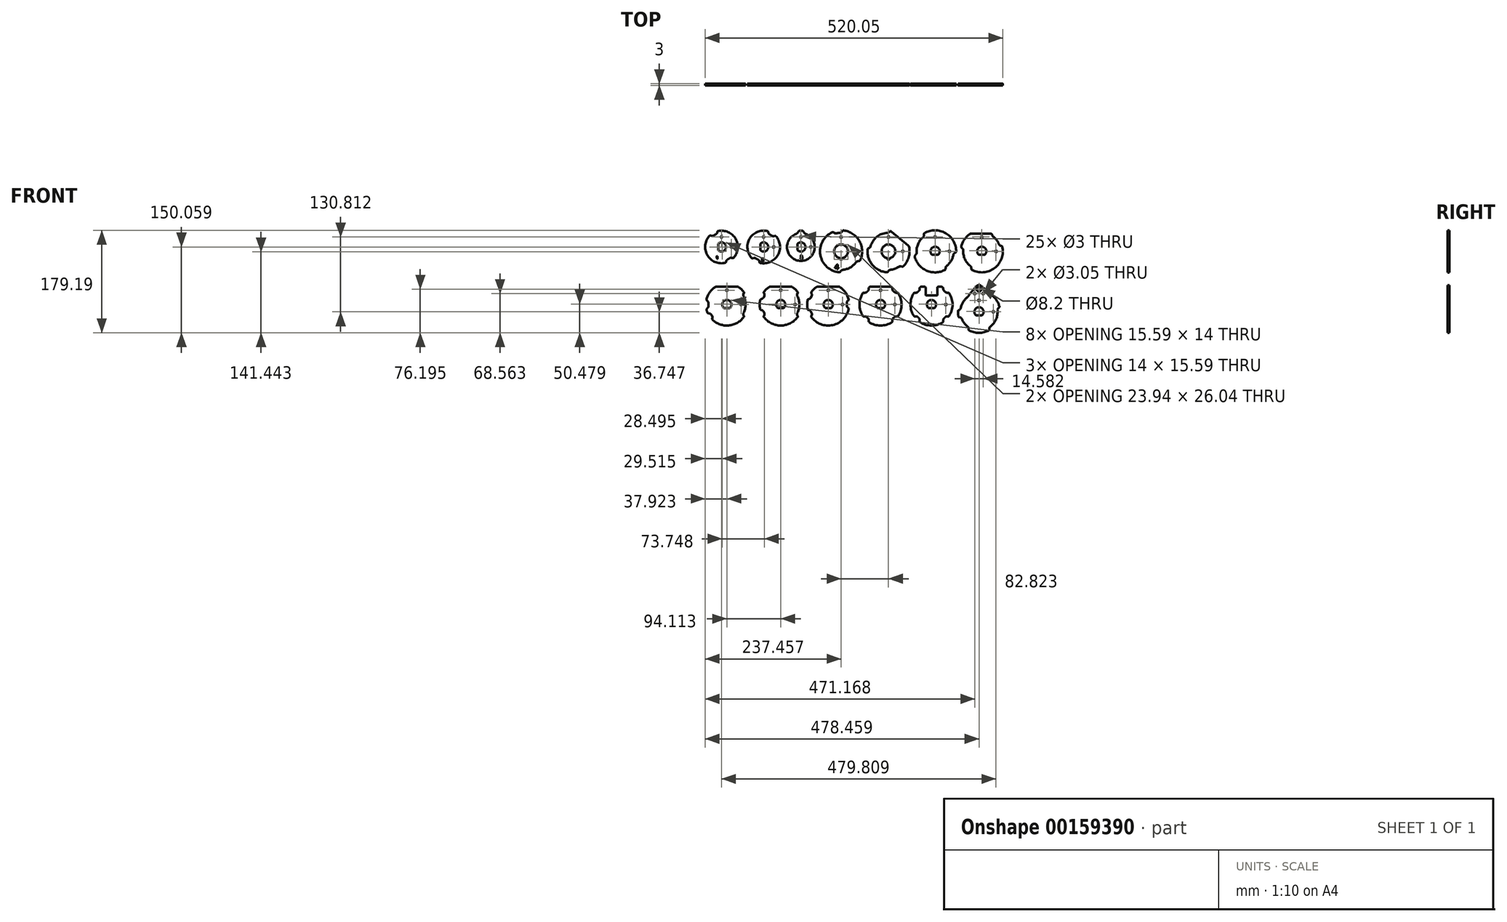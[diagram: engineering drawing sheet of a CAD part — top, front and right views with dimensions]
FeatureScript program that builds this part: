
annotation { "Feature Type Name" : "Feature", "Feature Type Description" : "" }
export const myFeature = defineFeature(function(context is Context, id is Id, definition is map)
    precondition{}
    {
        {
            var Q0;
            Q0=qCreatedBy(makeId("Front.planeOp"),FACE);
            var sketch = newSketch(context, id + "F0", { "sketchPlane" : qUnion([Q0])});
            skArc(sketch, "E0", {"start": v(14198.4, 8014.46) * mm, "mid": v(14188.74, 8004.94) * mm, "end": v(14183.2, 7992.56) * mm});
            skArc(sketch, "E1", {"start": v(14183.2, 7992.56) * mm, "mid": v(14183.2, 7992.07) * mm, "end": v(14183.43, 7991.64) * mm});
            skLineSegment(sketch, "E2", {"start": v(14183.43, 7991.64) * mm, "end": v(14185.45, 7989.48) * mm});
            skArc(sketch, "E3", {"start": v(14185.45, 7989.48) * mm, "mid": v(14186.3, 7988.07) * mm, "end": v(14186.52, 7986.44) * mm});
            skArc(sketch, "E4", {"start": v(14186.52, 7986.44) * mm, "mid": v(14186.42, 7983.83) * mm, "end": v(14186.54, 7981.21) * mm});
            skArc(sketch, "E5", {"start": v(14186.54, 7981.21) * mm, "mid": v(14186.34, 7979.58) * mm, "end": v(14185.5, 7978.17) * mm});
            skLineSegment(sketch, "E6", {"start": v(14185.5, 7978.17) * mm, "end": v(14183.5, 7975.98) * mm});
            skArc(sketch, "E7", {"start": v(14183.5, 7975.98) * mm, "mid": v(14183.27, 7975.55) * mm, "end": v(14183.27, 7975.07) * mm});
            skArc(sketch, "E8", {"start": v(14183.27, 7975.07) * mm, "mid": v(14184.12, 7972.16) * mm, "end": v(14185.22, 7969.33) * mm});
            skArc(sketch, "E9", {"start": v(14185.22, 7969.33) * mm, "mid": v(14185.51, 7968.94) * mm, "end": v(14185.96, 7968.74) * mm});
            skLineSegment(sketch, "E10", {"start": v(14185.96, 7968.74) * mm, "end": v(14188.8, 7968.24) * mm});
            skArc(sketch, "E11", {"start": v(14188.8, 7968.24) * mm, "mid": v(14190.26, 7967.67) * mm, "end": v(14191.39, 7966.6) * mm});
            skLineSegment(sketch, "E12", {"start": v(14191.39, 7966.6) * mm, "end": v(14192.28, 7965.31) * mm});
            skLineSegment(sketch, "E13", {"start": v(14192.28, 7965.31) * mm, "end": v(14193.18, 7964.04) * mm});
            skArc(sketch, "E14", {"start": v(14193.18, 7964.04) * mm, "mid": v(14193.8, 7962.6) * mm, "end": v(14193.84, 7961.05) * mm});
            skLineSegment(sketch, "E15", {"start": v(14193.84, 7961.05) * mm, "end": v(14193.34, 7958.2) * mm});
            skArc(sketch, "E16", {"start": v(14193.34, 7958.2) * mm, "mid": v(14193.37, 7957.71) * mm, "end": v(14193.64, 7957.3) * mm});
            skArc(sketch, "E17", {"start": v(14193.64, 7957.3) * mm, "mid": v(14222.13, 7947.36) * mm, "end": v(14248.46, 7962.1) * mm});
            skArc(sketch, "E18", {"start": v(14248.46, 7962.1) * mm, "mid": v(14248.64, 7962.55) * mm, "end": v(14248.6, 7963.04) * mm});
            skLineSegment(sketch, "E19", {"start": v(14248.6, 7963.04) * mm, "end": v(14247.58, 7965.82) * mm});
            skArc(sketch, "E20", {"start": v(14247.58, 7965.82) * mm, "mid": v(14247.35, 7967.45) * mm, "end": v(14247.79, 7969.03) * mm});
            skArc(sketch, "E21", {"start": v(14247.79, 7969.03) * mm, "mid": v(14251.42, 7983.97) * mm, "end": v(14247.79, 7998.9) * mm});
            skArc(sketch, "E22", {"start": v(14247.79, 7998.9) * mm, "mid": v(14247.35, 8000.5) * mm, "end": v(14247.58, 8002.12) * mm});
            skLineSegment(sketch, "E23", {"start": v(14247.58, 8002.12) * mm, "end": v(14248.6, 8004.9) * mm});
            skArc(sketch, "E24", {"start": v(14248.6, 8004.9) * mm, "mid": v(14248.64, 8005.39) * mm, "end": v(14248.46, 8005.84) * mm});
            skArc(sketch, "E25", {"start": v(14248.46, 8005.84) * mm, "mid": v(14244.32, 8010.53) * mm, "end": v(14239.44, 8014.46) * mm});
            skArc(sketch, "E26", {"start": v(14239.44, 8014.46) * mm, "mid": v(14238.64, 8014.84) * mm, "end": v(14237.77, 8014.97) * mm});
            skLineSegment(sketch, "E27", {"start": v(14237.77, 8014.97) * mm, "end": v(14200.08, 8014.97) * mm});
            skArc(sketch, "E28", {"start": v(14200.08, 8014.97) * mm, "mid": v(14199.2, 8014.84) * mm, "end": v(14198.4, 8014.46) * mm});
            skArc(sketch, "E29", {"start": v(14375.48, 8014.46) * mm, "mid": v(14370.6, 8010.53) * mm, "end": v(14366.46, 8005.83) * mm});
            skArc(sketch, "E30", {"start": v(14366.46, 8005.83) * mm, "mid": v(14366.27, 8005.38) * mm, "end": v(14366.32, 8004.9) * mm});
            skLineSegment(sketch, "E31", {"start": v(14366.32, 8004.9) * mm, "end": v(14367.31, 8002.18) * mm});
            skArc(sketch, "E32", {"start": v(14367.31, 8002.18) * mm, "mid": v(14367.55, 8000.64) * mm, "end": v(14367.18, 7999.12) * mm});
            skLineSegment(sketch, "E33", {"start": v(14367.18, 7999.12) * mm, "end": v(14366.52, 7997.7) * mm});
            skLineSegment(sketch, "E34", {"start": v(14366.52, 7997.7) * mm, "end": v(14365.86, 7996.29) * mm});
            skArc(sketch, "E35", {"start": v(14365.86, 7996.29) * mm, "mid": v(14364.94, 7995.03) * mm, "end": v(14363.6, 7994.22) * mm});
            skLineSegment(sketch, "E36", {"start": v(14363.6, 7994.22) * mm, "end": v(14360.89, 7993.23) * mm});
            skArc(sketch, "E37", {"start": v(14360.89, 7993.23) * mm, "mid": v(14360.48, 7992.96) * mm, "end": v(14360.26, 7992.53) * mm});
            skArc(sketch, "E38", {"start": v(14360.26, 7992.53) * mm, "mid": v(14359.25, 7983.96) * mm, "end": v(14360.26, 7975.4) * mm});
            skArc(sketch, "E39", {"start": v(14360.26, 7975.4) * mm, "mid": v(14360.49, 7974.97) * mm, "end": v(14360.9, 7974.7) * mm});
            skLineSegment(sketch, "E40", {"start": v(14360.9, 7974.7) * mm, "end": v(14363.6, 7973.7) * mm});
            skArc(sketch, "E41", {"start": v(14363.6, 7973.7) * mm, "mid": v(14364.94, 7972.9) * mm, "end": v(14365.86, 7971.63) * mm});
            skLineSegment(sketch, "E42", {"start": v(14365.86, 7971.63) * mm, "end": v(14366.52, 7970.22) * mm});
            skLineSegment(sketch, "E43", {"start": v(14366.52, 7970.22) * mm, "end": v(14367.18, 7968.8) * mm});
            skArc(sketch, "E44", {"start": v(14367.18, 7968.8) * mm, "mid": v(14367.55, 7967.29) * mm, "end": v(14367.31, 7965.75) * mm});
            skLineSegment(sketch, "E45", {"start": v(14367.31, 7965.75) * mm, "end": v(14366.33, 7963.04) * mm});
            skArc(sketch, "E46", {"start": v(14366.33, 7963.04) * mm, "mid": v(14366.28, 7962.55) * mm, "end": v(14366.46, 7962.1) * mm});
            skArc(sketch, "E47", {"start": v(14366.46, 7962.1) * mm, "mid": v(14403.79, 7948.05) * mm, "end": v(14431.94, 7976.3) * mm});
            skArc(sketch, "E48", {"start": v(14431.94, 7976.3) * mm, "mid": v(14431.92, 7976.79) * mm, "end": v(14431.67, 7977.21) * mm});
            skLineSegment(sketch, "E49", {"start": v(14431.67, 7977.21) * mm, "end": v(14429.7, 7979.1) * mm});
            skArc(sketch, "E50", {"start": v(14429.7, 7979.1) * mm, "mid": v(14428.73, 7980.52) * mm, "end": v(14428.45, 7982.21) * mm});
            skArc(sketch, "E51", {"start": v(14428.45, 7982.21) * mm, "mid": v(14428.5, 7984.33) * mm, "end": v(14428.4, 7986.45) * mm});
            skArc(sketch, "E52", {"start": v(14428.4, 7986.45) * mm, "mid": v(14428.62, 7988.07) * mm, "end": v(14429.47, 7989.48) * mm});
            skLineSegment(sketch, "E53", {"start": v(14429.47, 7989.48) * mm, "end": v(14431.49, 7991.65) * mm});
            skArc(sketch, "E54", {"start": v(14431.49, 7991.65) * mm, "mid": v(14431.72, 7992.07) * mm, "end": v(14431.73, 7992.56) * mm});
            skArc(sketch, "E55", {"start": v(14431.73, 7992.56) * mm, "mid": v(14426.18, 8004.94) * mm, "end": v(14416.52, 8014.46) * mm});
            skArc(sketch, "E56", {"start": v(14416.52, 8014.46) * mm, "mid": v(14415.72, 8014.84) * mm, "end": v(14414.84, 8014.97) * mm});
            skLineSegment(sketch, "E57", {"start": v(14414.84, 8014.97) * mm, "end": v(14377.16, 8014.97) * mm});
            skArc(sketch, "E58", {"start": v(14377.16, 8014.97) * mm, "mid": v(14376.28, 8014.84) * mm, "end": v(14375.48, 8014.46) * mm});
            skCircle(sketch, "E59", {"center": v(14659.46, 8010.7) * mm, "radius": 4.1 * mm});
            skCircle(sketch, "E60", {"center": v(14652.17, 8003.07) * mm, "radius": 1.52 * mm});
            skCircle(sketch, "E61", {"center": v(14666.75, 8003.07) * mm, "radius": 1.52 * mm});
            skArc(sketch, "E62", {"start": v(14350.95, 8112.94) * mm, "mid": v(14348.24, 8113.07) * mm, "end": v(14345.54, 8112.94) * mm});
            skArc(sketch, "E63", {"start": v(14345.54, 8112.94) * mm, "mid": v(14345.17, 8112.83) * mm, "end": v(14344.87, 8112.59) * mm});
            skLineSegment(sketch, "E64", {"start": v(14344.87, 8112.59) * mm, "end": v(14341.4, 8108.45) * mm});
            skArc(sketch, "E65", {"start": v(14341.4, 8108.45) * mm, "mid": v(14340.65, 8107.76) * mm, "end": v(14339.74, 8107.28) * mm});
            skArc(sketch, "E66", {"start": v(14339.74, 8107.28) * mm, "mid": v(14348.24, 8060.32) * mm, "end": v(14356.75, 8107.28) * mm});
            skArc(sketch, "E67", {"start": v(14356.75, 8107.28) * mm, "mid": v(14355.84, 8107.76) * mm, "end": v(14355.09, 8108.45) * mm});
            skLineSegment(sketch, "E68", {"start": v(14355.09, 8108.45) * mm, "end": v(14351.62, 8112.59) * mm});
            skArc(sketch, "E69", {"start": v(14351.62, 8112.59) * mm, "mid": v(14351.32, 8112.83) * mm, "end": v(14350.95, 8112.94) * mm});
            skCircle(sketch, "E70", {"center": v(14365.74, 8084.57) * mm, "radius": 1.5 * mm});
            skCircle(sketch, "E71", {"center": v(14348.24, 8102.07) * mm, "radius": 1.5 * mm});
            skArc(sketch, "E72", {"start": v(14273.41, 8062.4) * mm, "mid": v(14271.49, 8063.36) * mm, "end": v(14269.65, 8064.49) * mm});
            skArc(sketch, "E73", {"start": v(14269.65, 8064.49) * mm, "mid": v(14268.1, 8065.11) * mm, "end": v(14266.44, 8065.05) * mm});
            skLineSegment(sketch, "E74", {"start": v(14266.44, 8065.05) * mm, "end": v(14263.8, 8064.4) * mm});
            skArc(sketch, "E75", {"start": v(14263.8, 8064.4) * mm, "mid": v(14263.29, 8064.4) * mm, "end": v(14262.84, 8064.67) * mm});
            skArc(sketch, "E76", {"start": v(14262.84, 8064.67) * mm, "mid": v(14258.56, 8098.82) * mm, "end": v(14290.28, 8112.19) * mm});
            skArc(sketch, "E77", {"start": v(14290.28, 8112.19) * mm, "mid": v(14290.73, 8111.94) * mm, "end": v(14291, 8111.5) * mm});
            skLineSegment(sketch, "E78", {"start": v(14291, 8111.5) * mm, "end": v(14291.74, 8108.88) * mm});
            skArc(sketch, "E79", {"start": v(14291.74, 8108.88) * mm, "mid": v(14292.53, 8107.4) * mm, "end": v(14293.84, 8106.38) * mm});
            skArc(sketch, "E80", {"start": v(14293.84, 8106.38) * mm, "mid": v(14295.73, 8105.36) * mm, "end": v(14297.53, 8104.17) * mm});
            skArc(sketch, "E81", {"start": v(14297.53, 8104.17) * mm, "mid": v(14299.05, 8103.49) * mm, "end": v(14300.71, 8103.49) * mm});
            skLineSegment(sketch, "E82", {"start": v(14300.71, 8103.49) * mm, "end": v(14303.38, 8104.05) * mm});
            skArc(sketch, "E83", {"start": v(14303.38, 8104.05) * mm, "mid": v(14303.9, 8104.03) * mm, "end": v(14304.33, 8103.75) * mm});
            skArc(sketch, "E84", {"start": v(14304.33, 8103.75) * mm, "mid": v(14307.93, 8070.32) * mm, "end": v(14277.18, 8056.72) * mm});
            skArc(sketch, "E85", {"start": v(14277.18, 8056.72) * mm, "mid": v(14276.72, 8056.96) * mm, "end": v(14276.44, 8057.4) * mm});
            skLineSegment(sketch, "E86", {"start": v(14276.44, 8057.4) * mm, "end": v(14275.6, 8059.98) * mm});
            skArc(sketch, "E87", {"start": v(14275.6, 8059.98) * mm, "mid": v(14274.76, 8061.42) * mm, "end": v(14273.41, 8062.4) * mm});
            skArc(sketch, "E88", {"start": v(14503.45, 8065.13) * mm, "mid": v(14503.34, 8065.06) * mm, "end": v(14503.3, 8064.93) * mm});
            skLineSegment(sketch, "E89", {"start": v(14503.3, 8064.93) * mm, "end": v(14503.3, 8062.93) * mm});
            skLineSegment(sketch, "E90", {"start": v(14503.3, 8062.93) * mm, "end": v(14499.27, 8062.93) * mm});
            skLineSegment(sketch, "E91", {"start": v(14499.27, 8062.93) * mm, "end": v(14499.27, 8064.93) * mm});
            skArc(sketch, "E92", {"start": v(14499.27, 8064.93) * mm, "mid": v(14499.22, 8065.06) * mm, "end": v(14499.1, 8065.13) * mm});
            skArc(sketch, "E93", {"start": v(14499.1, 8065.13) * mm, "mid": v(14501.28, 8088.97) * mm, "end": v(14503.45, 8065.13) * mm});
            skArc(sketch, "E94", {"start": v(14464.73, 8080.78) * mm, "mid": v(14473.13, 8053.33) * mm, "end": v(14498.7, 8040.3) * mm});
            skArc(sketch, "E95", {"start": v(14498.7, 8040.3) * mm, "mid": v(14499.18, 8040.38) * mm, "end": v(14499.57, 8040.68) * mm});
            skLineSegment(sketch, "E96", {"start": v(14499.57, 8040.68) * mm, "end": v(14501.37, 8043.03) * mm});
            skArc(sketch, "E97", {"start": v(14501.37, 8043.03) * mm, "mid": v(14502.62, 8044.1) * mm, "end": v(14504.19, 8044.58) * mm});
            skArc(sketch, "E98", {"start": v(14504.19, 8044.58) * mm, "mid": v(14512.4, 8046.41) * mm, "end": v(14519.86, 8050.29) * mm});
            skArc(sketch, "E99", {"start": v(14519.86, 8050.29) * mm, "mid": v(14521.37, 8050.93) * mm, "end": v(14523.01, 8050.91) * mm});
            skLineSegment(sketch, "E100", {"start": v(14523.01, 8050.91) * mm, "end": v(14525.9, 8050.27) * mm});
            skArc(sketch, "E101", {"start": v(14525.9, 8050.27) * mm, "mid": v(14526.4, 8050.28) * mm, "end": v(14526.82, 8050.53) * mm});
            skArc(sketch, "E102", {"start": v(14526.82, 8050.53) * mm, "mid": v(14536.53, 8066.56) * mm, "end": v(14537.07, 8085.3) * mm});
            skArc(sketch, "E103", {"start": v(14537.07, 8085.3) * mm, "mid": v(14536.7, 8086.19) * mm, "end": v(14536.08, 8086.92) * mm});
            skLineSegment(sketch, "E104", {"start": v(14536.08, 8086.92) * mm, "end": v(14506.99, 8111.32) * mm});
            skArc(sketch, "E105", {"start": v(14506.99, 8111.32) * mm, "mid": v(14504.8, 8112.02) * mm, "end": v(14502.76, 8110.96) * mm});
            skLineSegment(sketch, "E106", {"start": v(14502.76, 8110.96) * mm, "end": v(14502.67, 8110.84) * mm});
            skArc(sketch, "E107", {"start": v(14502.67, 8110.84) * mm, "mid": v(14501.38, 8109.83) * mm, "end": v(14499.79, 8109.42) * mm});
            skArc(sketch, "E108", {"start": v(14499.79, 8109.42) * mm, "mid": v(14480.94, 8102.3) * mm, "end": v(14469.9, 8085.44) * mm});
            skArc(sketch, "E109", {"start": v(14469.9, 8085.44) * mm, "mid": v(14469.16, 8083.97) * mm, "end": v(14467.9, 8082.93) * mm});
            skLineSegment(sketch, "E110", {"start": v(14467.9, 8082.93) * mm, "end": v(14465.26, 8081.56) * mm});
            skArc(sketch, "E111", {"start": v(14465.26, 8081.56) * mm, "mid": v(14464.9, 8081.24) * mm, "end": v(14464.73, 8080.78) * mm});
            skArc(sketch, "E112", {"start": v(14416.28, 8065.13) * mm, "mid": v(14418.46, 8088.97) * mm, "end": v(14420.63, 8065.13) * mm});
            skArc(sketch, "E113", {"start": v(14420.63, 8065.13) * mm, "mid": v(14420.51, 8065.06) * mm, "end": v(14420.47, 8064.93) * mm});
            skLineSegment(sketch, "E114", {"start": v(14420.47, 8064.93) * mm, "end": v(14420.47, 8062.93) * mm});
            skLineSegment(sketch, "E115", {"start": v(14420.47, 8062.93) * mm, "end": v(14416.45, 8062.93) * mm});
            skLineSegment(sketch, "E116", {"start": v(14416.45, 8062.93) * mm, "end": v(14416.45, 8064.93) * mm});
            skArc(sketch, "E117", {"start": v(14416.45, 8064.93) * mm, "mid": v(14416.4, 8065.06) * mm, "end": v(14416.28, 8065.13) * mm});
            skArc(sketch, "E118", {"start": v(14416.96, 8109.42) * mm, "mid": v(14418.55, 8109.83) * mm, "end": v(14419.85, 8110.84) * mm});
            skLineSegment(sketch, "E119", {"start": v(14419.85, 8110.84) * mm, "end": v(14421.75, 8113.11) * mm});
            skArc(sketch, "E120", {"start": v(14421.75, 8113.11) * mm, "mid": v(14422.15, 8113.4) * mm, "end": v(14422.63, 8113.46) * mm});
            skArc(sketch, "E121", {"start": v(14422.63, 8113.46) * mm, "mid": v(14450.68, 8094.63) * mm, "end": v(14451.5, 8060.85) * mm});
            skArc(sketch, "E122", {"start": v(14451.5, 8060.85) * mm, "mid": v(14451.18, 8060.48) * mm, "end": v(14450.73, 8060.3) * mm});
            skLineSegment(sketch, "E123", {"start": v(14450.73, 8060.3) * mm, "end": v(14447.79, 8059.91) * mm});
            skArc(sketch, "E124", {"start": v(14447.79, 8059.91) * mm, "mid": v(14446.24, 8059.37) * mm, "end": v(14445.04, 8058.25) * mm});
            skArc(sketch, "E125", {"start": v(14445.04, 8058.25) * mm, "mid": v(14434.7, 8048.8) * mm, "end": v(14421.36, 8044.58) * mm});
            skArc(sketch, "E126", {"start": v(14421.36, 8044.58) * mm, "mid": v(14419.8, 8044.1) * mm, "end": v(14418.55, 8043.03) * mm});
            skLineSegment(sketch, "E127", {"start": v(14418.55, 8043.03) * mm, "end": v(14416.74, 8040.68) * mm});
            skArc(sketch, "E128", {"start": v(14416.74, 8040.68) * mm, "mid": v(14416.36, 8040.38) * mm, "end": v(14415.88, 8040.3) * mm});
            skArc(sketch, "E129", {"start": v(14415.88, 8040.3) * mm, "mid": v(14382.27, 8070.57) * mm, "end": v(14403.5, 8110.52) * mm});
            skArc(sketch, "E130", {"start": v(14403.5, 8110.52) * mm, "mid": v(14403.98, 8110.6) * mm, "end": v(14404.44, 8110.45) * mm});
            skLineSegment(sketch, "E131", {"start": v(14404.44, 8110.45) * mm, "end": v(14406.94, 8108.86) * mm});
            skArc(sketch, "E132", {"start": v(14406.94, 8108.86) * mm, "mid": v(14408.48, 8108.28) * mm, "end": v(14410.12, 8108.36) * mm});
            skArc(sketch, "E133", {"start": v(14410.12, 8108.36) * mm, "mid": v(14413.51, 8109.07) * mm, "end": v(14416.96, 8109.42) * mm});
            skCircle(sketch, "E134", {"center": v(14443.46, 8076.95) * mm, "radius": 1.5 * mm});
            skCircle(sketch, "E135", {"center": v(14418.46, 8101.95) * mm, "radius": 1.5 * mm});
            skLineSegment(sketch, "E136", {"start": v(14331.88, 8014.97) * mm, "end": v(14294.2, 8014.97) * mm});
            skArc(sketch, "E137", {"start": v(14294.2, 8014.97) * mm, "mid": v(14293.32, 8014.84) * mm, "end": v(14292.52, 8014.46) * mm});
            skArc(sketch, "E138", {"start": v(14292.52, 8014.46) * mm, "mid": v(14287.64, 8010.53) * mm, "end": v(14283.5, 8005.83) * mm});
            skArc(sketch, "E139", {"start": v(14283.5, 8005.83) * mm, "mid": v(14283.31, 8005.38) * mm, "end": v(14283.36, 8004.9) * mm});
            skLineSegment(sketch, "E140", {"start": v(14283.36, 8004.9) * mm, "end": v(14284.35, 8002.18) * mm});
            skArc(sketch, "E141", {"start": v(14284.35, 8002.18) * mm, "mid": v(14284.59, 8000.64) * mm, "end": v(14284.22, 7999.12) * mm});
            skLineSegment(sketch, "E142", {"start": v(14284.22, 7999.12) * mm, "end": v(14283.56, 7997.7) * mm});
            skLineSegment(sketch, "E143", {"start": v(14283.56, 7997.7) * mm, "end": v(14282.9, 7996.29) * mm});
            skArc(sketch, "E144", {"start": v(14282.9, 7996.29) * mm, "mid": v(14281.98, 7995.03) * mm, "end": v(14280.64, 7994.22) * mm});
            skLineSegment(sketch, "E145", {"start": v(14280.64, 7994.22) * mm, "end": v(14277.93, 7993.23) * mm});
            skArc(sketch, "E146", {"start": v(14277.93, 7993.23) * mm, "mid": v(14277.52, 7992.96) * mm, "end": v(14277.3, 7992.53) * mm});
            skArc(sketch, "E147", {"start": v(14277.3, 7992.53) * mm, "mid": v(14276.29, 7983.96) * mm, "end": v(14277.3, 7975.4) * mm});
            skArc(sketch, "E148", {"start": v(14277.3, 7975.4) * mm, "mid": v(14277.53, 7974.97) * mm, "end": v(14277.93, 7974.7) * mm});
            skLineSegment(sketch, "E149", {"start": v(14277.93, 7974.7) * mm, "end": v(14280.64, 7973.7) * mm});
            skArc(sketch, "E150", {"start": v(14280.64, 7973.7) * mm, "mid": v(14281.98, 7972.9) * mm, "end": v(14282.9, 7971.63) * mm});
            skLineSegment(sketch, "E151", {"start": v(14282.9, 7971.63) * mm, "end": v(14283.56, 7970.22) * mm});
            skLineSegment(sketch, "E152", {"start": v(14283.56, 7970.22) * mm, "end": v(14284.22, 7968.8) * mm});
            skArc(sketch, "E153", {"start": v(14284.22, 7968.8) * mm, "mid": v(14284.59, 7967.29) * mm, "end": v(14284.35, 7965.75) * mm});
            skLineSegment(sketch, "E154", {"start": v(14284.35, 7965.75) * mm, "end": v(14283.36, 7963.04) * mm});
            skArc(sketch, "E155", {"start": v(14283.36, 7963.04) * mm, "mid": v(14283.31, 7962.55) * mm, "end": v(14283.5, 7962.1) * mm});
            skArc(sketch, "E156", {"start": v(14283.5, 7962.1) * mm, "mid": v(14313.04, 7947.22) * mm, "end": v(14342.57, 7962.1) * mm});
            skArc(sketch, "E157", {"start": v(14342.57, 7962.1) * mm, "mid": v(14342.76, 7962.55) * mm, "end": v(14342.7, 7963.04) * mm});
            skLineSegment(sketch, "E158", {"start": v(14342.7, 7963.04) * mm, "end": v(14341.7, 7965.82) * mm});
            skArc(sketch, "E159", {"start": v(14341.7, 7965.82) * mm, "mid": v(14341.46, 7967.45) * mm, "end": v(14341.9, 7969.03) * mm});
            skArc(sketch, "E160", {"start": v(14341.9, 7969.03) * mm, "mid": v(14345.54, 7983.97) * mm, "end": v(14341.9, 7998.9) * mm});
            skArc(sketch, "E161", {"start": v(14341.9, 7998.9) * mm, "mid": v(14341.46, 8000.5) * mm, "end": v(14341.7, 8002.12) * mm});
            skLineSegment(sketch, "E162", {"start": v(14341.7, 8002.12) * mm, "end": v(14342.7, 8004.9) * mm});
            skArc(sketch, "E163", {"start": v(14342.7, 8004.9) * mm, "mid": v(14342.76, 8005.39) * mm, "end": v(14342.57, 8005.84) * mm});
            skArc(sketch, "E164", {"start": v(14342.57, 8005.84) * mm, "mid": v(14338.43, 8010.53) * mm, "end": v(14333.55, 8014.46) * mm});
            skArc(sketch, "E165", {"start": v(14333.55, 8014.46) * mm, "mid": v(14332.76, 8014.84) * mm, "end": v(14331.88, 8014.97) * mm});
            skArc(sketch, "E166", {"start": v(14511.36, 8005.98) * mm, "mid": v(14510.43, 8006.95) * mm, "end": v(14509.46, 8007.88) * mm});
            skArc(sketch, "E167", {"start": v(14509.46, 8007.88) * mm, "mid": v(14508.4, 8009.52) * mm, "end": v(14508.23, 8011.48) * mm});
            skArc(sketch, "E168", {"start": v(14508.23, 8011.48) * mm, "mid": v(14507.56, 8013.9) * mm, "end": v(14505.27, 8014.97) * mm});
            skLineSegment(sketch, "E169", {"start": v(14505.27, 8014.97) * mm, "end": v(14469.64, 8014.97) * mm});
            skArc(sketch, "E170", {"start": v(14469.64, 8014.97) * mm, "mid": v(14467.35, 8013.9) * mm, "end": v(14466.68, 8011.48) * mm});
            skArc(sketch, "E171", {"start": v(14466.68, 8011.48) * mm, "mid": v(14466.51, 8009.52) * mm, "end": v(14465.44, 8007.88) * mm});
            skArc(sketch, "E172", {"start": v(14465.44, 8007.88) * mm, "mid": v(14464.47, 8006.95) * mm, "end": v(14463.54, 8005.98) * mm});
            skArc(sketch, "E173", {"start": v(14463.54, 8005.98) * mm, "mid": v(14462.2, 8005.03) * mm, "end": v(14460.6, 8004.69) * mm});
            skLineSegment(sketch, "E174", {"start": v(14460.6, 8004.69) * mm, "end": v(14457.63, 8004.69) * mm});
            skArc(sketch, "E175", {"start": v(14457.63, 8004.69) * mm, "mid": v(14457.16, 8004.57) * mm, "end": v(14456.8, 8004.24) * mm});
            skArc(sketch, "E176", {"start": v(14456.8, 8004.24) * mm, "mid": v(14450.7, 7983.97) * mm, "end": v(14456.8, 7963.7) * mm});
            skArc(sketch, "E177", {"start": v(14456.8, 7963.7) * mm, "mid": v(14457.16, 7963.37) * mm, "end": v(14457.63, 7963.25) * mm});
            skLineSegment(sketch, "E178", {"start": v(14457.63, 7963.25) * mm, "end": v(14460.6, 7963.25) * mm});
            skArc(sketch, "E179", {"start": v(14460.6, 7963.25) * mm, "mid": v(14462.2, 7962.91) * mm, "end": v(14463.54, 7961.96) * mm});
            skArc(sketch, "E180", {"start": v(14463.54, 7961.96) * mm, "mid": v(14464.47, 7960.99) * mm, "end": v(14465.44, 7960.06) * mm});
            skArc(sketch, "E181", {"start": v(14465.44, 7960.06) * mm, "mid": v(14466.4, 7958.72) * mm, "end": v(14466.73, 7957.12) * mm});
            skLineSegment(sketch, "E182", {"start": v(14466.73, 7957.12) * mm, "end": v(14466.73, 7954.15) * mm});
            skArc(sketch, "E183", {"start": v(14466.73, 7954.15) * mm, "mid": v(14466.85, 7953.68) * mm, "end": v(14467.18, 7953.32) * mm});
            skArc(sketch, "E184", {"start": v(14467.18, 7953.32) * mm, "mid": v(14487.45, 7947.22) * mm, "end": v(14507.72, 7953.32) * mm});
            skArc(sketch, "E185", {"start": v(14507.72, 7953.32) * mm, "mid": v(14508.05, 7953.68) * mm, "end": v(14508.17, 7954.15) * mm});
            skLineSegment(sketch, "E186", {"start": v(14508.17, 7954.15) * mm, "end": v(14508.17, 7957.12) * mm});
            skArc(sketch, "E187", {"start": v(14508.17, 7957.12) * mm, "mid": v(14508.5, 7958.72) * mm, "end": v(14509.46, 7960.06) * mm});
            skArc(sketch, "E188", {"start": v(14509.46, 7960.06) * mm, "mid": v(14510.43, 7960.99) * mm, "end": v(14511.36, 7961.96) * mm});
            skArc(sketch, "E189", {"start": v(14511.36, 7961.96) * mm, "mid": v(14512.7, 7962.91) * mm, "end": v(14514.3, 7963.25) * mm});
            skLineSegment(sketch, "E190", {"start": v(14514.3, 7963.25) * mm, "end": v(14517.27, 7963.25) * mm});
            skArc(sketch, "E191", {"start": v(14517.27, 7963.25) * mm, "mid": v(14517.74, 7963.37) * mm, "end": v(14518.1, 7963.7) * mm});
            skArc(sketch, "E192", {"start": v(14518.1, 7963.7) * mm, "mid": v(14524.2, 7983.97) * mm, "end": v(14518.1, 8004.24) * mm});
            skArc(sketch, "E193", {"start": v(14518.1, 8004.24) * mm, "mid": v(14517.74, 8004.57) * mm, "end": v(14517.27, 8004.69) * mm});
            skLineSegment(sketch, "E194", {"start": v(14517.27, 8004.69) * mm, "end": v(14514.3, 8004.69) * mm});
            skArc(sketch, "E195", {"start": v(14514.3, 8004.69) * mm, "mid": v(14512.7, 8005.03) * mm, "end": v(14511.36, 8005.98) * mm});
            skArc(sketch, "E196", {"start": v(14554.44, 8007.88) * mm, "mid": v(14553.47, 8006.95) * mm, "end": v(14552.54, 8005.98) * mm});
            skArc(sketch, "E197", {"start": v(14552.54, 8005.98) * mm, "mid": v(14551.2, 8005.03) * mm, "end": v(14549.6, 8004.69) * mm});
            skLineSegment(sketch, "E198", {"start": v(14549.6, 8004.69) * mm, "end": v(14546.64, 8004.69) * mm});
            skArc(sketch, "E199", {"start": v(14546.64, 8004.69) * mm, "mid": v(14546.16, 8004.57) * mm, "end": v(14545.8, 8004.24) * mm});
            skArc(sketch, "E200", {"start": v(14545.8, 8004.24) * mm, "mid": v(14539.7, 7983.97) * mm, "end": v(14545.8, 7963.7) * mm});
            skArc(sketch, "E201", {"start": v(14545.8, 7963.7) * mm, "mid": v(14546.16, 7963.37) * mm, "end": v(14546.64, 7963.25) * mm});
            skLineSegment(sketch, "E202", {"start": v(14546.64, 7963.25) * mm, "end": v(14549.6, 7963.25) * mm});
            skArc(sketch, "E203", {"start": v(14549.6, 7963.25) * mm, "mid": v(14551.2, 7962.91) * mm, "end": v(14552.54, 7961.96) * mm});
            skArc(sketch, "E204", {"start": v(14552.54, 7961.96) * mm, "mid": v(14553.47, 7960.99) * mm, "end": v(14554.44, 7960.06) * mm});
            skArc(sketch, "E205", {"start": v(14554.44, 7960.06) * mm, "mid": v(14555.4, 7958.72) * mm, "end": v(14555.73, 7957.12) * mm});
            skLineSegment(sketch, "E206", {"start": v(14555.73, 7957.12) * mm, "end": v(14555.73, 7954.15) * mm});
            skArc(sketch, "E207", {"start": v(14555.73, 7954.15) * mm, "mid": v(14555.85, 7953.68) * mm, "end": v(14556.18, 7953.32) * mm});
            skArc(sketch, "E208", {"start": v(14556.18, 7953.32) * mm, "mid": v(14576.46, 7947.22) * mm, "end": v(14596.73, 7953.32) * mm});
            skArc(sketch, "E209", {"start": v(14596.73, 7953.32) * mm, "mid": v(14597.06, 7953.68) * mm, "end": v(14597.18, 7954.15) * mm});
            skLineSegment(sketch, "E210", {"start": v(14597.18, 7954.15) * mm, "end": v(14597.18, 7957.12) * mm});
            skArc(sketch, "E211", {"start": v(14597.18, 7957.12) * mm, "mid": v(14597.51, 7958.72) * mm, "end": v(14598.47, 7960.06) * mm});
            skArc(sketch, "E212", {"start": v(14598.47, 7960.06) * mm, "mid": v(14599.44, 7960.99) * mm, "end": v(14600.37, 7961.96) * mm});
            skArc(sketch, "E213", {"start": v(14600.37, 7961.96) * mm, "mid": v(14601.7, 7962.91) * mm, "end": v(14603.3, 7963.25) * mm});
            skLineSegment(sketch, "E214", {"start": v(14603.3, 7963.25) * mm, "end": v(14606.27, 7963.25) * mm});
            skArc(sketch, "E215", {"start": v(14606.27, 7963.25) * mm, "mid": v(14606.75, 7963.37) * mm, "end": v(14607.1, 7963.7) * mm});
            skArc(sketch, "E216", {"start": v(14607.1, 7963.7) * mm, "mid": v(14613.2, 7983.97) * mm, "end": v(14607.1, 8004.24) * mm});
            skArc(sketch, "E217", {"start": v(14607.1, 8004.24) * mm, "mid": v(14606.75, 8004.57) * mm, "end": v(14606.27, 8004.69) * mm});
            skLineSegment(sketch, "E218", {"start": v(14606.27, 8004.69) * mm, "end": v(14603.3, 8004.69) * mm});
            skArc(sketch, "E219", {"start": v(14603.3, 8004.69) * mm, "mid": v(14601.7, 8005.03) * mm, "end": v(14600.37, 8005.98) * mm});
            skArc(sketch, "E220", {"start": v(14600.37, 8005.98) * mm, "mid": v(14599.44, 8006.95) * mm, "end": v(14598.47, 8007.88) * mm});
            skArc(sketch, "E221", {"start": v(14598.47, 8007.88) * mm, "mid": v(14597.5, 8009.25) * mm, "end": v(14597.18, 8010.9) * mm});
            skArc(sketch, "E222", {"start": v(14597.18, 8010.9) * mm, "mid": v(14596.03, 8013.77) * mm, "end": v(14593.18, 8014.97) * mm});
            skLineSegment(sketch, "E223", {"start": v(14593.18, 8014.97) * mm, "end": v(14588.46, 8014.97) * mm});
            skArc(sketch, "E224", {"start": v(14588.46, 8014.97) * mm, "mid": v(14587.04, 8014.38) * mm, "end": v(14586.46, 8012.97) * mm});
            skLineSegment(sketch, "E225", {"start": v(14586.46, 8012.97) * mm, "end": v(14586.46, 8000.17) * mm});
            skArc(sketch, "E226", {"start": v(14586.46, 8000.17) * mm, "mid": v(14586.4, 8000.03) * mm, "end": v(14586.26, 7999.97) * mm});
            skLineSegment(sketch, "E227", {"start": v(14586.26, 7999.97) * mm, "end": v(14566.66, 7999.97) * mm});
            skArc(sketch, "E228", {"start": v(14566.66, 7999.97) * mm, "mid": v(14566.51, 8000.03) * mm, "end": v(14566.46, 8000.17) * mm});
            skLineSegment(sketch, "E229", {"start": v(14566.46, 8000.17) * mm, "end": v(14566.46, 8012.97) * mm});
            skArc(sketch, "E230", {"start": v(14566.46, 8012.97) * mm, "mid": v(14565.87, 8014.38) * mm, "end": v(14564.46, 8014.97) * mm});
            skLineSegment(sketch, "E231", {"start": v(14564.46, 8014.97) * mm, "end": v(14558.64, 8014.97) * mm});
            skArc(sketch, "E232", {"start": v(14558.64, 8014.97) * mm, "mid": v(14556.35, 8013.9) * mm, "end": v(14555.68, 8011.48) * mm});
            skArc(sketch, "E233", {"start": v(14555.68, 8011.48) * mm, "mid": v(14555.52, 8009.52) * mm, "end": v(14554.44, 8007.88) * mm});
            skArc(sketch, "E234", {"start": v(14679.3, 7945.52) * mm, "mid": v(14689.2, 7958.17) * mm, "end": v(14691.84, 7974.01) * mm});
            skArc(sketch, "E235", {"start": v(14691.84, 7974.01) * mm, "mid": v(14692.04, 7975.64) * mm, "end": v(14692.88, 7977.05) * mm});
            skLineSegment(sketch, "E236", {"start": v(14692.88, 7977.05) * mm, "end": v(14694.88, 7979.24) * mm});
            skArc(sketch, "E237", {"start": v(14694.88, 7979.24) * mm, "mid": v(14695.11, 7979.67) * mm, "end": v(14695.11, 7980.16) * mm});
            skArc(sketch, "E238", {"start": v(14695.11, 7980.16) * mm, "mid": v(14690.39, 7991.1) * mm, "end": v(14682.4, 7999.96) * mm});
            skLineSegment(sketch, "E239", {"start": v(14682.4, 7999.96) * mm, "end": v(14664.65, 8015.4) * mm});
            skArc(sketch, "E240", {"start": v(14664.65, 8015.4) * mm, "mid": v(14659.3, 8017.7) * mm, "end": v(14654.06, 8015.16) * mm});
            skLineSegment(sketch, "E241", {"start": v(14654.06, 8015.16) * mm, "end": v(14641.45, 7999.9) * mm});
            skArc(sketch, "E242", {"start": v(14641.45, 7999.9) * mm, "mid": v(14641.3, 7999.68) * mm, "end": v(14641.21, 7999.43) * mm});
            skArc(sketch, "E243", {"start": v(14641.21, 7999.43) * mm, "mid": v(14640.68, 7998.13) * mm, "end": v(14639.73, 7997.08) * mm});
            skArc(sketch, "E244", {"start": v(14639.73, 7997.08) * mm, "mid": v(14631.88, 7988.45) * mm, "end": v(14627.58, 7977.6) * mm});
            skArc(sketch, "E245", {"start": v(14627.58, 7977.6) * mm, "mid": v(14626.85, 7975.96) * mm, "end": v(14625.47, 7974.8) * mm});
            skLineSegment(sketch, "E246", {"start": v(14625.47, 7974.8) * mm, "end": v(14623.29, 7973.7) * mm});
            skArc(sketch, "E247", {"start": v(14623.29, 7973.7) * mm, "mid": v(14622.9, 7973.34) * mm, "end": v(14622.74, 7972.85) * mm});
            skArc(sketch, "E248", {"start": v(14622.74, 7972.85) * mm, "mid": v(14622.88, 7967.73) * mm, "end": v(14623.72, 7962.7) * mm});
            skArc(sketch, "E249", {"start": v(14623.72, 7962.7) * mm, "mid": v(14623.95, 7962.26) * mm, "end": v(14624.35, 7961.98) * mm});
            skLineSegment(sketch, "E250", {"start": v(14624.35, 7961.98) * mm, "end": v(14627.14, 7960.97) * mm});
            skArc(sketch, "E251", {"start": v(14627.14, 7960.97) * mm, "mid": v(14628.53, 7960.1) * mm, "end": v(14629.46, 7958.75) * mm});
            skArc(sketch, "E252", {"start": v(14629.46, 7958.75) * mm, "mid": v(14633.67, 7951.47) * mm, "end": v(14639.61, 7945.52) * mm});
            skArc(sketch, "E253", {"start": v(14639.61, 7945.52) * mm, "mid": v(14640.68, 7944.27) * mm, "end": v(14641.16, 7942.7) * mm});
            skLineSegment(sketch, "E254", {"start": v(14641.16, 7942.7) * mm, "end": v(14641.42, 7939.75) * mm});
            skArc(sketch, "E255", {"start": v(14641.42, 7939.75) * mm, "mid": v(14641.58, 7939.29) * mm, "end": v(14641.93, 7938.95) * mm});
            skArc(sketch, "E256", {"start": v(14641.93, 7938.95) * mm, "mid": v(14659.46, 7934.5) * mm, "end": v(14676.98, 7938.95) * mm});
            skArc(sketch, "E257", {"start": v(14676.98, 7938.95) * mm, "mid": v(14677.34, 7939.28) * mm, "end": v(14677.5, 7939.75) * mm});
            skLineSegment(sketch, "E258", {"start": v(14677.5, 7939.75) * mm, "end": v(14677.76, 7942.7) * mm});
            skArc(sketch, "E259", {"start": v(14677.76, 7942.7) * mm, "mid": v(14678.24, 7944.27) * mm, "end": v(14679.3, 7945.52) * mm});
            skArc(sketch, "E260", {"start": v(14644.45, 8051.22) * mm, "mid": v(14645.52, 8049.97) * mm, "end": v(14646, 8048.4) * mm});
            skLineSegment(sketch, "E261", {"start": v(14646, 8048.4) * mm, "end": v(14646.26, 8045.44) * mm});
            skArc(sketch, "E262", {"start": v(14646.26, 8045.44) * mm, "mid": v(14646.42, 8044.98) * mm, "end": v(14646.77, 8044.65) * mm});
            skArc(sketch, "E263", {"start": v(14646.77, 8044.65) * mm, "mid": v(14686.67, 8047.8) * mm, "end": v(14700.04, 8085.52) * mm});
            skArc(sketch, "E264", {"start": v(14700.04, 8085.52) * mm, "mid": v(14699.81, 8085.95) * mm, "end": v(14699.41, 8086.23) * mm});
            skLineSegment(sketch, "E265", {"start": v(14699.41, 8086.23) * mm, "end": v(14696.62, 8087.24) * mm});
            skArc(sketch, "E266", {"start": v(14696.62, 8087.24) * mm, "mid": v(14695.23, 8088.1) * mm, "end": v(14694.3, 8089.46) * mm});
            skArc(sketch, "E267", {"start": v(14694.3, 8089.46) * mm, "mid": v(14690.09, 8096.74) * mm, "end": v(14684.15, 8102.69) * mm});
            skArc(sketch, "E268", {"start": v(14684.15, 8102.69) * mm, "mid": v(14683.12, 8103.86) * mm, "end": v(14682.63, 8105.34) * mm});
            skArc(sketch, "E269", {"start": v(14682.63, 8105.34) * mm, "mid": v(14681.63, 8107.2) * mm, "end": v(14679.65, 8107.96) * mm});
            skLineSegment(sketch, "E270", {"start": v(14679.65, 8107.96) * mm, "end": v(14645.45, 8107.96) * mm});
            skArc(sketch, "E271", {"start": v(14645.45, 8107.96) * mm, "mid": v(14644.57, 8107.82) * mm, "end": v(14643.77, 8107.44) * mm});
            skArc(sketch, "E272", {"start": v(14643.77, 8107.44) * mm, "mid": v(14633.93, 8097.66) * mm, "end": v(14628.42, 8084.92) * mm});
            skArc(sketch, "E273", {"start": v(14628.42, 8084.92) * mm, "mid": v(14628.43, 8084.43) * mm, "end": v(14628.68, 8084) * mm});
            skLineSegment(sketch, "E274", {"start": v(14628.68, 8084) * mm, "end": v(14630.74, 8081.87) * mm});
            skArc(sketch, "E275", {"start": v(14630.74, 8081.87) * mm, "mid": v(14631.61, 8080.48) * mm, "end": v(14631.86, 8078.86) * mm});
            skArc(sketch, "E276", {"start": v(14631.86, 8078.86) * mm, "mid": v(14634.73, 8063.48) * mm, "end": v(14644.45, 8051.22) * mm});
            skArc(sketch, "E277", {"start": v(14602.64, 8051.21) * mm, "mid": v(14610.58, 8060.1) * mm, "end": v(14614.78, 8071.23) * mm});
            skArc(sketch, "E278", {"start": v(14614.78, 8071.23) * mm, "mid": v(14615.4, 8072.76) * mm, "end": v(14616.57, 8073.9) * mm});
            skLineSegment(sketch, "E279", {"start": v(14616.57, 8073.9) * mm, "end": v(14619.07, 8075.5) * mm});
            skArc(sketch, "E280", {"start": v(14619.07, 8075.5) * mm, "mid": v(14619.4, 8075.85) * mm, "end": v(14619.54, 8076.32) * mm});
            skArc(sketch, "E281", {"start": v(14619.54, 8076.32) * mm, "mid": v(14601.17, 8108.78) * mm, "end": v(14563.87, 8108.46) * mm});
            skArc(sketch, "E282", {"start": v(14563.87, 8108.46) * mm, "mid": v(14563.53, 8108.11) * mm, "end": v(14563.39, 8107.65) * mm});
            skLineSegment(sketch, "E283", {"start": v(14563.39, 8107.65) * mm, "end": v(14563.26, 8104.68) * mm});
            skArc(sketch, "E284", {"start": v(14563.26, 8104.68) * mm, "mid": v(14562.85, 8103.1) * mm, "end": v(14561.84, 8101.8) * mm});
            skArc(sketch, "E285", {"start": v(14561.84, 8101.8) * mm, "mid": v(14552.82, 8089.52) * mm, "end": v(14550.39, 8074.48) * mm});
            skArc(sketch, "E286", {"start": v(14550.39, 8074.48) * mm, "mid": v(14550.17, 8072.85) * mm, "end": v(14549.32, 8071.44) * mm});
            skLineSegment(sketch, "E287", {"start": v(14549.32, 8071.44) * mm, "end": v(14547.3, 8069.28) * mm});
            skArc(sketch, "E288", {"start": v(14547.3, 8069.28) * mm, "mid": v(14547.07, 8068.85) * mm, "end": v(14547.06, 8068.36) * mm});
            skArc(sketch, "E289", {"start": v(14547.06, 8068.36) * mm, "mid": v(14567.84, 8043.38) * mm, "end": v(14600.32, 8044.65) * mm});
            skArc(sketch, "E290", {"start": v(14600.32, 8044.65) * mm, "mid": v(14600.67, 8044.98) * mm, "end": v(14600.83, 8045.44) * mm});
            skLineSegment(sketch, "E291", {"start": v(14600.83, 8045.44) * mm, "end": v(14601.1, 8048.4) * mm});
            skArc(sketch, "E292", {"start": v(14601.1, 8048.4) * mm, "mid": v(14601.57, 8049.97) * mm, "end": v(14602.64, 8051.21) * mm});
            skCircle(sketch, "E293", {"center": v(14300.74, 8084.57) * mm, "radius": 1.5 * mm});
            skCircle(sketch, "E294", {"center": v(14283.24, 8102.07) * mm, "radius": 1.5 * mm});
            skCircle(sketch, "E295", {"center": v(14659.46, 7991.26) * mm, "radius": 1.5 * mm});
            skCircle(sketch, "E296", {"center": v(14526.28, 8076.95) * mm, "radius": 1.5 * mm});
            skCircle(sketch, "E297", {"center": v(14501.28, 8101.95) * mm, "radius": 1.5 * mm});
            skCircle(sketch, "E298", {"center": v(14607.8, 8076.95) * mm, "radius": 1.5 * mm});
            skCircle(sketch, "E299", {"center": v(14582.8, 8101.95) * mm, "radius": 1.5 * mm});
            skCircle(sketch, "E300", {"center": v(14689.3, 8076.95) * mm, "radius": 1.5 * mm});
            skCircle(sketch, "E301", {"center": v(14664.3, 8101.95) * mm, "radius": 1.5 * mm});
            skCircle(sketch, "E302", {"center": v(14684.46, 7971.26) * mm, "radius": 1.5 * mm});
            skCircle(sketch, "E303", {"center": v(14601.46, 7983.97) * mm, "radius": 1.5 * mm});
            skCircle(sketch, "E304", {"center": v(14512.45, 7983.97) * mm, "radius": 1.5 * mm});
            skCircle(sketch, "E305", {"center": v(14487.45, 8008.97) * mm, "radius": 1.5 * mm});
            skCircle(sketch, "E306", {"center": v(14421, 7983.97) * mm, "radius": 1.5 * mm});
            skCircle(sketch, "E307", {"center": v(14396, 8008.97) * mm, "radius": 1.5 * mm});
            skCircle(sketch, "E308", {"center": v(14338.04, 7983.97) * mm, "radius": 1.5 * mm});
            skCircle(sketch, "E309", {"center": v(14313.04, 8008.97) * mm, "radius": 1.5 * mm});
            skCircle(sketch, "E310", {"center": v(14243.92, 7983.97) * mm, "radius": 1.5 * mm});
            skCircle(sketch, "E311", {"center": v(14218.92, 8008.97) * mm, "radius": 1.5 * mm});
            skArc(sketch, "E312", {"start": v(14277.26, 8079.22) * mm, "mid": v(14291.26, 8084.57) * mm, "end": v(14277.26, 8089.91) * mm});
            skLineSegment(sketch, "E313", {"start": v(14277.26, 8079.22) * mm, "end": v(14277.26, 8089.91) * mm});
            skArc(sketch, "E314", {"start": v(14342.26, 8079.22) * mm, "mid": v(14356.26, 8084.57) * mm, "end": v(14342.26, 8089.91) * mm});
            skLineSegment(sketch, "E315", {"start": v(14342.26, 8079.22) * mm, "end": v(14342.26, 8089.91) * mm});
            skArc(sketch, "E316", {"start": v(14588.14, 8070.97) * mm, "mid": v(14582.8, 8084.97) * mm, "end": v(14577.45, 8070.97) * mm});
            skLineSegment(sketch, "E317", {"start": v(14577.45, 8070.97) * mm, "end": v(14588.14, 8070.97) * mm});
            skArc(sketch, "E318", {"start": v(14669.64, 8070.98) * mm, "mid": v(14664.3, 8084.98) * mm, "end": v(14658.96, 8070.98) * mm});
            skLineSegment(sketch, "E319", {"start": v(14658.96, 8070.98) * mm, "end": v(14669.64, 8070.98) * mm});
            skArc(sketch, "E320", {"start": v(14664.8, 7965.28) * mm, "mid": v(14659.46, 7979.28) * mm, "end": v(14654.11, 7965.28) * mm});
            skLineSegment(sketch, "E321", {"start": v(14654.11, 7965.28) * mm, "end": v(14664.8, 7965.28) * mm});
            skArc(sketch, "E322", {"start": v(14581.8, 7977.99) * mm, "mid": v(14576.46, 7991.99) * mm, "end": v(14571.11, 7977.99) * mm});
            skLineSegment(sketch, "E323", {"start": v(14571.11, 7977.99) * mm, "end": v(14581.8, 7977.99) * mm});
            skArc(sketch, "E324", {"start": v(14492.8, 7977.99) * mm, "mid": v(14487.45, 7991.99) * mm, "end": v(14482.1, 7977.99) * mm});
            skLineSegment(sketch, "E325", {"start": v(14482.1, 7977.99) * mm, "end": v(14492.8, 7977.99) * mm});
            skArc(sketch, "E326", {"start": v(14401.34, 7977.99) * mm, "mid": v(14396, 7991.99) * mm, "end": v(14390.65, 7977.99) * mm});
            skLineSegment(sketch, "E327", {"start": v(14390.65, 7977.99) * mm, "end": v(14401.34, 7977.99) * mm});
            skArc(sketch, "E328", {"start": v(14318.38, 7977.99) * mm, "mid": v(14313.04, 7991.99) * mm, "end": v(14307.7, 7977.99) * mm});
            skLineSegment(sketch, "E329", {"start": v(14307.7, 7977.99) * mm, "end": v(14318.38, 7977.99) * mm});
            skArc(sketch, "E330", {"start": v(14224.27, 7977.99) * mm, "mid": v(14218.92, 7991.99) * mm, "end": v(14213.58, 7977.99) * mm});
            skLineSegment(sketch, "E331", {"start": v(14213.58, 7977.99) * mm, "end": v(14224.27, 7977.99) * mm});
            skArc(sketch, "E332", {"start": v(14220.1, 8062.76) * mm, "mid": v(14218.78, 8061.73) * mm, "end": v(14218, 8060.26) * mm});
            skLineSegment(sketch, "E333", {"start": v(14218, 8060.26) * mm, "end": v(14217.25, 8057.64) * mm});
            skArc(sketch, "E334", {"start": v(14217.25, 8057.64) * mm, "mid": v(14216.98, 8057.2) * mm, "end": v(14216.53, 8056.95) * mm});
            skArc(sketch, "E335", {"start": v(14216.53, 8056.95) * mm, "mid": v(14184.81, 8070.32) * mm, "end": v(14189.1, 8104.47) * mm});
            skArc(sketch, "E336", {"start": v(14189.1, 8104.47) * mm, "mid": v(14189.54, 8104.74) * mm, "end": v(14190.05, 8104.74) * mm});
            skLineSegment(sketch, "E337", {"start": v(14190.05, 8104.74) * mm, "end": v(14192.7, 8104.08) * mm});
            skArc(sketch, "E338", {"start": v(14192.7, 8104.08) * mm, "mid": v(14194.36, 8104.03) * mm, "end": v(14195.9, 8104.65) * mm});
            skArc(sketch, "E339", {"start": v(14195.9, 8104.65) * mm, "mid": v(14197.74, 8105.78) * mm, "end": v(14199.66, 8106.74) * mm});
            skArc(sketch, "E340", {"start": v(14199.66, 8106.74) * mm, "mid": v(14201.01, 8107.71) * mm, "end": v(14201.85, 8109.16) * mm});
            skLineSegment(sketch, "E341", {"start": v(14201.85, 8109.16) * mm, "end": v(14202.69, 8111.75) * mm});
            skArc(sketch, "E342", {"start": v(14202.69, 8111.75) * mm, "mid": v(14202.97, 8112.18) * mm, "end": v(14203.43, 8112.42) * mm});
            skArc(sketch, "E343", {"start": v(14203.43, 8112.42) * mm, "mid": v(14234.18, 8098.82) * mm, "end": v(14230.58, 8065.4) * mm});
            skArc(sketch, "E344", {"start": v(14230.58, 8065.4) * mm, "mid": v(14230.14, 8065.11) * mm, "end": v(14229.63, 8065.09) * mm});
            skLineSegment(sketch, "E345", {"start": v(14229.63, 8065.09) * mm, "end": v(14226.97, 8065.65) * mm});
            skArc(sketch, "E346", {"start": v(14226.97, 8065.65) * mm, "mid": v(14225.3, 8065.65) * mm, "end": v(14223.78, 8064.97) * mm});
            skArc(sketch, "E347", {"start": v(14223.78, 8064.97) * mm, "mid": v(14221.98, 8063.78) * mm, "end": v(14220.1, 8062.76) * mm});
            skCircle(sketch, "E348", {"center": v(14227, 8084.57) * mm, "radius": 1.5 * mm});
            skCircle(sketch, "E349", {"center": v(14209.5, 8102.07) * mm, "radius": 1.5 * mm});
            skArc(sketch, "E350", {"start": v(14203.52, 8079.22) * mm, "mid": v(14217.52, 8084.57) * mm, "end": v(14203.52, 8089.91) * mm});
            skLineSegment(sketch, "E351", {"start": v(14203.52, 8079.22) * mm, "end": v(14203.52, 8089.91) * mm});
            skSolve(sketch);
        }
        {
            var Q0;
            Q0 = qSketchRegion(id + "F0", true);
            extrude(context, id + "F1", {"entities" : qUnion([Q0]), "depth" : 3 * mm, "offsetDistance" : 25 * mm, "symmetric" : true});
        }
        {
            var Q0;
            Q0=makeQuery(id+"F1.opExtrude","CAP_FACE",FACE,{"disambiguationData":[OSD([sQuery(id+"F0.wireOp",EDGE,"E332"),sQuery(id+"F0.wireOp",EDGE,"E333"),sQuery(id+"F0.wireOp",EDGE,"E334"),sQuery(id+"F0.wireOp",EDGE,"E335"),sQuery(id+"F0.wireOp",EDGE,"E336"),sQuery(id+"F0.wireOp",EDGE,"E337"),sQuery(id+"F0.wireOp",EDGE,"E338"),sQuery(id+"F0.wireOp",EDGE,"E339"),sQuery(id+"F0.wireOp",EDGE,"E340"),sQuery(id+"F0.wireOp",EDGE,"E341"),sQuery(id+"F0.wireOp",EDGE,"E342"),sQuery(id+"F0.wireOp",EDGE,"E343"),sQuery(id+"F0.wireOp",EDGE,"E344"),sQuery(id+"F0.wireOp",EDGE,"E345"),sQuery(id+"F0.wireOp",EDGE,"E346"),sQuery(id+"F0.wireOp",EDGE,"E347"),sQuery(id+"F0.wireOp",EDGE,"E348"),sQuery(id+"F0.wireOp",EDGE,"E349"),sQuery(id+"F0.wireOp",EDGE,"E350"),sQuery(id+"F0.wireOp",EDGE,"E351")])],"isStart":false});
            var sketch = newSketch(context, id + "F2", { "sketchPlane" : qUnion([Q0])});
            skText(sketch, "E352", { "text": "1", "fontName": "OpenSans-Bold.ttf"});
            skText(sketch, "E353", { "text": "2", "fontName": "OpenSans-Bold.ttf"});
            skText(sketch, "E354", { "text": "3", "fontName": "OpenSans-Bold.ttf"});
            skText(sketch, "E355", { "text": "4", "fontName": "OpenSans-Bold.ttf"});
            const initialGuessF2  = {"E352": [14.19968, 8.06352, 1, 0, 0.00531], "E353": [14.27936, 8.05888, 1, 0, 0.0055], "E354": [14.34689, 8.06402, 1, 0, 0.00554], "E355": [14.40749, 8.04576, 1, 0, 0.00826]};
            skSetInitialGuess(sketch, initialGuessF2);
            skSolve(sketch);
        }
        {
            var Q0;
            Q0 = qSketchRegion(id + "F2", true);
            extrude(context, id + "F3", {"entities" : qUnion([Q0]), "operationType" : NewBodyOperationType.REMOVE, "oppositeDirection" : true, "depth" : 0.2 * mm, "offsetDistance" : 25 * mm});
        }
    });
